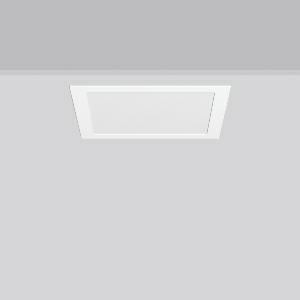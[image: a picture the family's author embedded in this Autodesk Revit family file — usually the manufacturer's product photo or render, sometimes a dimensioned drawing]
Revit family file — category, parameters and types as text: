
# Revit family: toledo_flat_square_e_901488_002_c862
name_source: partatom
category: Lighting Fixtures
units: mm (PartAtom-declared; Revit-internal decimal feet)

## family parameters
Cut with Voids When Loaded = No
Host = Face
Light Source = No
Part Type = Normal
Room Calculation Point = No
Round Connector Dimension = Use Diameter
Shared = No

## types (1)
- TOLEDO FLAT square E (1 x LED Modul 830, 2150 lm, 3000)
    Apparent Load = 21 VA
    CIE Flux Codes = 48 80 96 100 100
    Color Rendering = 80
    Color Temperature = 3000
    Default Elevation = 1800 mm
    Description = Series: TOLEDO FLAT square
Ultra thin recessed downlight. Housing: die-cast aluminium. Light guide and diffuser made of non-yellowing PMMA, opal matt. Ceiling installation with spring system. Mounting depth depends on ceiling strength. Suitable for through-wiring with separately available accessories. Surface mounted housing as accessory for all sizes. Retrofittable decorative cylinders made of chintz fabric as accessory, optional with satin finish plastic diffuser. Through-wiring box (5 pole) available as accessory. 
Colour: white
Length: 300 mm
Width: 300 mm
Height: 3 mm
Cut-out length: 280 mm
Cut-out width: 280 mm
Recess height: 31-56 mm
Luminaire: recess height: 31-51 mm
Lamp: LED
Socket: without socket
Colour temperature: 3000K
Colour rendering index (CRI): 80
System power: 21 W
Rated luminous flux: 2150 lm
Luminous efficiency: 102 lm/W
Control gear: Regulated power supply
Protection class: II
Type of protection: IP 54
    Height = 0 mm  [stored 0 ft]
    Lamp = 1 x LED Modul 830
    Lamp Light Flux = 2150 lm
    Lamp count = 1
    Length = 300 mm
    Lifetime = 50000 h
    Luminous efficacy = 102 lm/W
    Manufacturer = RZB
    ModVariant = No
    Model = 901488.002
    Mounting Place = Ceiling
    Mounting Type = Recessed
    Number of Poles = 1
    OnlyDefault = Yes
    Power Factor = 1
    Product Name = TOLEDO FLAT square E
    Product group = Recessed downlights
    ProductGroupID = 402
    Protection Class = Protection class II
    Protection Degree = IP 20
    RLX_Detail_Level = 1
    RLX_Emergency_Light_Flux = 0 lm
    RLX_Emergency_Type = 0
    RLX_Emergency_Type_DB = No
    RlxData = <blob elided: 60857 chars, md5=75390997>
    Socket = socket
    Standby Power = 0 W
    System Light Flux = 2150 lm
    System Power = 21 W
    Type Comments = Product without accessories
    Type Image = 901488.002.jpg
    URL = http://relux.com
    VarID = ---
    Voltage = 230 V
    Voltage Range = 220-240 V
    Weight = 0.00 kg
    Width = 300 mm

note: [stored X ft] marks values corroborated as IEEE doubles in the binary element streams (Revit-internal decimal feet)

## geometry (parser evidence)
native form markers: Blend x4, Sweep x9
no freeform markers — native parametric forms only
